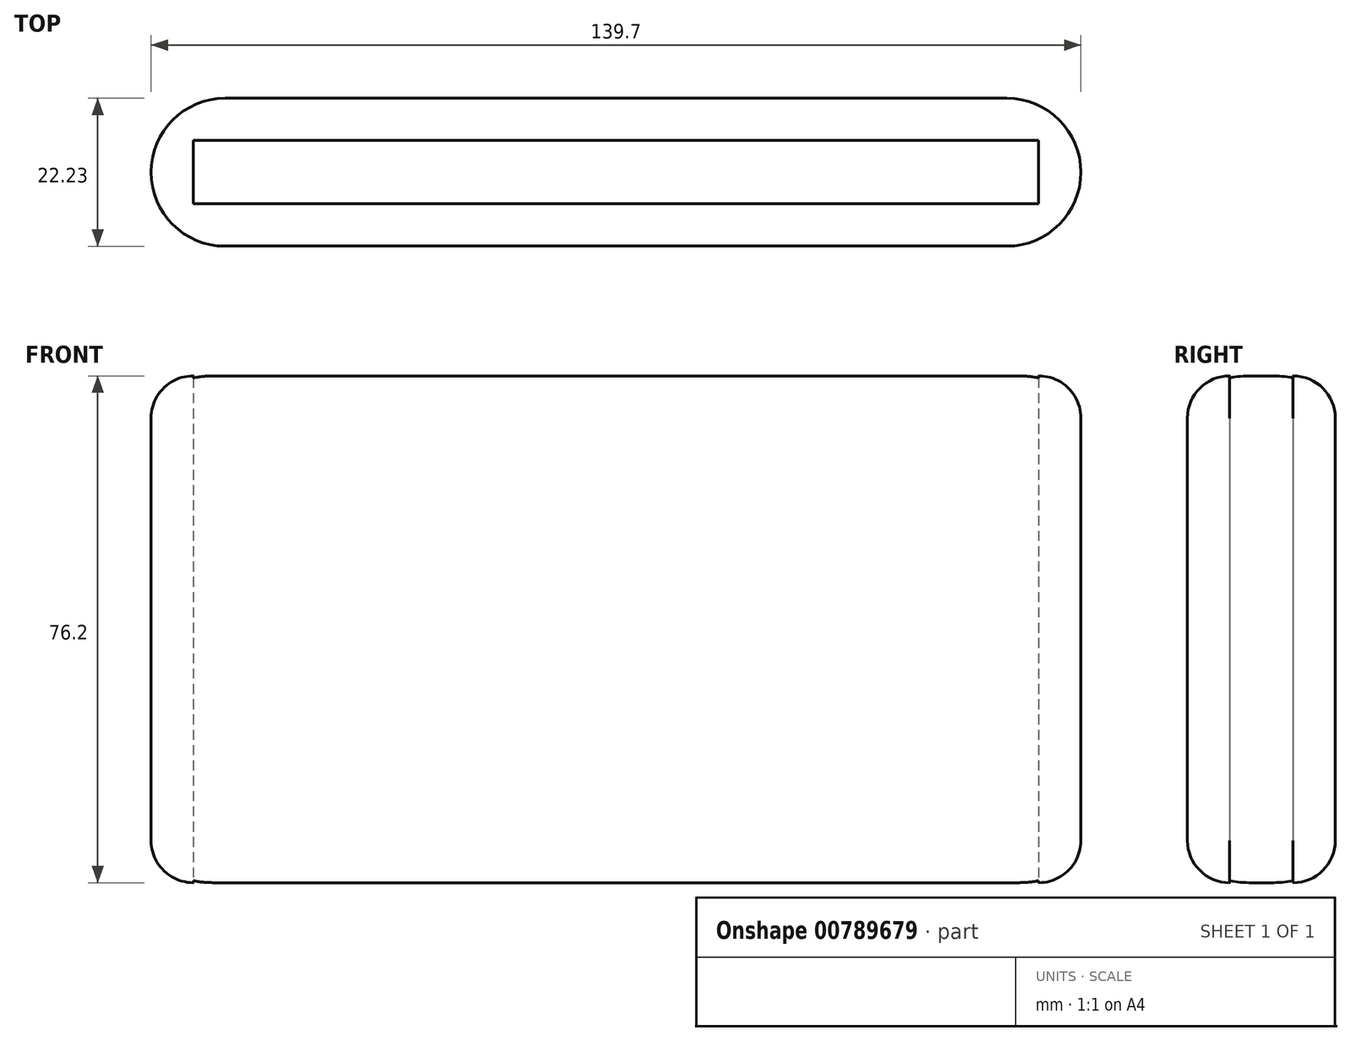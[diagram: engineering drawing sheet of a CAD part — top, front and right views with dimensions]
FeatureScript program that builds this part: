
annotation { "Feature Type Name" : "Feature", "Feature Type Description" : "" }
export const myFeature = defineFeature(function(context is Context, id is Id, definition is map)
    precondition{}
    {
        {
            var Q0;
            Q0=qCreatedBy(makeId("Top.planeOp"),FACE);
            var sketch = newSketch(context, id + "F0", { "sketchPlane" : qUnion([Q0])});
            skLineSegment(sketch, "E0.bottom", {"start": v(-65.67, -23.81) * mm, "end": v(61.33, -23.81) * mm});
            skLineSegment(sketch, "E0.top", {"start": v(-65.67, -33.34) * mm, "end": v(61.33, -33.34) * mm});
            skLineSegment(sketch, "E0.left", {"start": v(-65.67, -23.81) * mm, "end": v(-65.67, -33.34) * mm});
            skLineSegment(sketch, "E0.right", {"start": v(61.33, -23.81) * mm, "end": v(61.33, -33.34) * mm});
            skLineSegment(sketch, "E1.bottom", {"start": v(-72.02, -39.69) * mm, "end": v(67.68, -39.69) * mm});
            skLineSegment(sketch, "E1.top", {"start": v(-72.02, -17.46) * mm, "end": v(67.68, -17.46) * mm});
            skLineSegment(sketch, "E1.left", {"start": v(-72.02, -39.69) * mm, "end": v(-72.02, -17.46) * mm});
            skLineSegment(sketch, "E1.right", {"start": v(67.68, -39.69) * mm, "end": v(67.68, -17.46) * mm});
            skSolve(sketch);
        }
        {
            var Q0;
            Q0=makeQuery(id+"F0.imprint","IMPRINT",FACE,{"disambiguationData":[TD([[makeQuery(id+"F0.imprint","IMPRINT",EDGE,{"derivedFrom":sQuery(id+"F0.wireOp",EDGE,"E0.bottom")}),1.0]])]});
            extrude(context, id + "F1", {"entities" : qUnion([Q0]), "depth" : 76.2 * mm, "offsetDistance" : 25.4 * mm});
        }
        {
            var Q0;
            Q0=makeQuery(id+"F1.opExtrude","SWEPT_EDGE",EDGE,{"disambiguationData":[OSD([sQuery(id+"F0.wireOp",EDGE,"E1.bottom"),sQuery(id+"F0.wireOp",EDGE,"E1.left")])]});
            var Q1;
            Q1=makeQuery(id+"F1.opExtrude","SWEPT_EDGE",EDGE,{"disambiguationData":[OSD([sQuery(id+"F0.wireOp",EDGE,"E1.top"),sQuery(id+"F0.wireOp",EDGE,"E1.right")])]});
            var Q2;
            Q2=makeQuery(id+"F1.opExtrude","SWEPT_EDGE",EDGE,{"disambiguationData":[OSD([sQuery(id+"F0.wireOp",EDGE,"E1.bottom"),sQuery(id+"F0.wireOp",EDGE,"E1.right")])]});
            var Q3;
            Q3=makeQuery(id+"F1.opExtrude","SWEPT_EDGE",EDGE,{"disambiguationData":[OSD([sQuery(id+"F0.wireOp",EDGE,"E1.top"),sQuery(id+"F0.wireOp",EDGE,"E1.left")])]});
            fillet(context, id + "F2", {"entities" : qUnion([Q0, Q1, Q2, Q3]), "radius" : 11.1 * mm, "tangentPropagation" : true, "allowEdgeOverflow" : false});
        }
        {
            var Q0;
            {var subQ0=sQuery(id+"F0.wireOp",EDGE,"E1.left");var subQ1=sQuery(id+"F0.wireOp",EDGE,"E1.bottom");Q0=makeQuery(id+"F2.opFillet","BLEND_EDGE",EDGE,{"blendedFrom":[makeQuery(id+"F1.opExtrude","SWEPT_EDGE",EDGE,{"disambiguationData":[OSD([subQ1,subQ0])]}),makeQuery(id+"F1.opExtrude","CAP_FACE",FACE,{"disambiguationData":[OSD([sQuery(id+"F0.wireOp",EDGE,"E0.bottom"),sQuery(id+"F0.wireOp",EDGE,"E0.top"),sQuery(id+"F0.wireOp",EDGE,"E0.left"),sQuery(id+"F0.wireOp",EDGE,"E0.right"),subQ1,sQuery(id+"F0.wireOp",EDGE,"E1.top"),subQ0,sQuery(id+"F0.wireOp",EDGE,"E1.right")])],"isStart":false})],"blendedInto":[makeQuery(id+"F1.opExtrude","CAP_FACE",FACE,{"disambiguationData":[OSD([sQuery(id+"F0.wireOp",EDGE,"E0.bottom"),sQuery(id+"F0.wireOp",EDGE,"E0.top"),sQuery(id+"F0.wireOp",EDGE,"E0.left"),sQuery(id+"F0.wireOp",EDGE,"E0.right"),subQ1,sQuery(id+"F0.wireOp",EDGE,"E1.top"),subQ0,sQuery(id+"F0.wireOp",EDGE,"E1.right")])],"isStart":false})]});}
            var Q1;
            {var subQ0=sQuery(id+"F0.wireOp",EDGE,"E1.right");var subQ1=sQuery(id+"F0.wireOp",EDGE,"E1.top");Q1=makeQuery(id+"F2.opFillet","BLEND_EDGE",EDGE,{"blendedFrom":[makeQuery(id+"F1.opExtrude","SWEPT_EDGE",EDGE,{"disambiguationData":[OSD([subQ1,subQ0])]}),makeQuery(id+"F1.opExtrude","CAP_FACE",FACE,{"disambiguationData":[OSD([sQuery(id+"F0.wireOp",EDGE,"E0.bottom"),sQuery(id+"F0.wireOp",EDGE,"E0.top"),sQuery(id+"F0.wireOp",EDGE,"E0.left"),sQuery(id+"F0.wireOp",EDGE,"E0.right"),sQuery(id+"F0.wireOp",EDGE,"E1.bottom"),subQ1,sQuery(id+"F0.wireOp",EDGE,"E1.left"),subQ0])],"isStart":false})],"blendedInto":[makeQuery(id+"F1.opExtrude","CAP_FACE",FACE,{"disambiguationData":[OSD([sQuery(id+"F0.wireOp",EDGE,"E0.bottom"),sQuery(id+"F0.wireOp",EDGE,"E0.top"),sQuery(id+"F0.wireOp",EDGE,"E0.left"),sQuery(id+"F0.wireOp",EDGE,"E0.right"),sQuery(id+"F0.wireOp",EDGE,"E1.bottom"),subQ1,sQuery(id+"F0.wireOp",EDGE,"E1.left"),subQ0])],"isStart":false})]});}
            var Q2;
            {var subQ0=sQuery(id+"F0.wireOp",EDGE,"E1.right");var subQ1=sQuery(id+"F0.wireOp",EDGE,"E1.top");Q2=makeQuery(id+"F2.opFillet","BLEND_EDGE",EDGE,{"blendedFrom":[makeQuery(id+"F1.opExtrude","SWEPT_EDGE",EDGE,{"disambiguationData":[OSD([subQ1,subQ0])]}),makeQuery(id+"F1.opExtrude","CAP_FACE",FACE,{"disambiguationData":[OSD([sQuery(id+"F0.wireOp",EDGE,"E0.bottom"),sQuery(id+"F0.wireOp",EDGE,"E0.top"),sQuery(id+"F0.wireOp",EDGE,"E0.left"),sQuery(id+"F0.wireOp",EDGE,"E0.right"),sQuery(id+"F0.wireOp",EDGE,"E1.bottom"),subQ1,sQuery(id+"F0.wireOp",EDGE,"E1.left"),subQ0])],"isStart":true})],"blendedInto":[makeQuery(id+"F1.opExtrude","CAP_FACE",FACE,{"disambiguationData":[OSD([sQuery(id+"F0.wireOp",EDGE,"E0.bottom"),sQuery(id+"F0.wireOp",EDGE,"E0.top"),sQuery(id+"F0.wireOp",EDGE,"E0.left"),sQuery(id+"F0.wireOp",EDGE,"E0.right"),sQuery(id+"F0.wireOp",EDGE,"E1.bottom"),subQ1,sQuery(id+"F0.wireOp",EDGE,"E1.left"),subQ0])],"isStart":true})]});}
            var Q3;
            {var subQ0=sQuery(id+"F0.wireOp",EDGE,"E1.left");var subQ1=sQuery(id+"F0.wireOp",EDGE,"E1.bottom");Q3=makeQuery(id+"F2.opFillet","BLEND_EDGE",EDGE,{"blendedFrom":[makeQuery(id+"F1.opExtrude","SWEPT_EDGE",EDGE,{"disambiguationData":[OSD([subQ1,subQ0])]}),makeQuery(id+"F1.opExtrude","CAP_FACE",FACE,{"disambiguationData":[OSD([sQuery(id+"F0.wireOp",EDGE,"E0.bottom"),sQuery(id+"F0.wireOp",EDGE,"E0.top"),sQuery(id+"F0.wireOp",EDGE,"E0.left"),sQuery(id+"F0.wireOp",EDGE,"E0.right"),subQ1,sQuery(id+"F0.wireOp",EDGE,"E1.top"),subQ0,sQuery(id+"F0.wireOp",EDGE,"E1.right")])],"isStart":true})],"blendedInto":[makeQuery(id+"F1.opExtrude","CAP_FACE",FACE,{"disambiguationData":[OSD([sQuery(id+"F0.wireOp",EDGE,"E0.bottom"),sQuery(id+"F0.wireOp",EDGE,"E0.top"),sQuery(id+"F0.wireOp",EDGE,"E0.left"),sQuery(id+"F0.wireOp",EDGE,"E0.right"),subQ1,sQuery(id+"F0.wireOp",EDGE,"E1.top"),subQ0,sQuery(id+"F0.wireOp",EDGE,"E1.right")])],"isStart":true})]});}
            fillet(context, id + "F3", {"entities" : qUnion([Q0, Q1, Q2, Q3]), "radius" : 6.35 * mm, "tangentPropagation" : true, "allowEdgeOverflow" : false});
        }
    });
